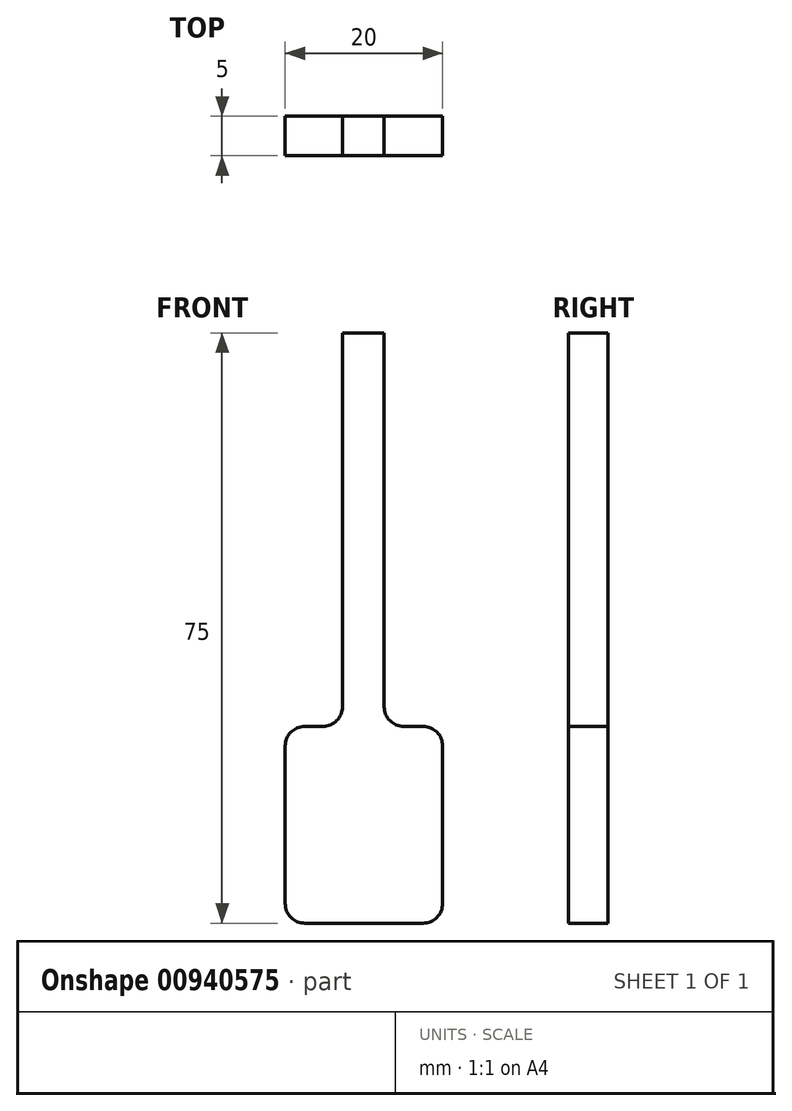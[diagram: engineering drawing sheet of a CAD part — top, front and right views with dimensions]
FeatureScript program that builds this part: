
annotation { "Feature Type Name" : "Feature", "Feature Type Description" : "" }
export const myFeature = defineFeature(function(context is Context, id is Id, definition is map)
    precondition{}
    {
        {
            var Q0;
            Q0=qCreatedBy(makeId("Front.planeOp"),FACE);
            var sketch = newSketch(context, id + "F0", { "sketchPlane" : qUnion([Q0])});
            skLineSegment(sketch, "E0.bottom", {"start": v(-7.5, -12.5) * mm, "end": v(7.5, -12.5) * mm});
            skLineSegment(sketch, "E0.left", {"start": v(-10, -10) * mm, "end": v(-10, 10) * mm});
            skLineSegment(sketch, "E0.right", {"start": v(10, -10) * mm, "end": v(10, 10) * mm});
            skPoint(sketch, "E0.middle", {"position": v(0, 0) * mm});
            skLineSegment(sketch, "E1.top", {"start": v(-2.72, 62.5) * mm, "end": v(2.57, 62.5) * mm});
            skLineSegment(sketch, "E1.left", {"start": v(-2.72, 15) * mm, "end": v(-2.72, 62.5) * mm});
            skLineSegment(sketch, "E1.right", {"start": v(2.57, 15) * mm, "end": v(2.57, 62.5) * mm});
            skLineSegment(sketch, "E2", {"start": v(-7.5, 12.5) * mm, "end": v(-5.22, 12.5) * mm});
            skLineSegment(sketch, "E3", {"start": v(5.07, 12.5) * mm, "end": v(7.5, 12.5) * mm});
            skPoint(sketch, "E4.visualSharp", {"position": v(-10, 12.5) * mm});
            skArc(sketch, "E4.filletArc", {"start": v(-7.5, 12.5) * mm, "mid": v(-9.27, 11.77) * mm, "end": v(-10, 10) * mm});
            skPoint(sketch, "E5.visualSharp", {"position": v(10, 12.5) * mm});
            skArc(sketch, "E5.filletArc", {"start": v(10, 10) * mm, "mid": v(9.27, 11.77) * mm, "end": v(7.5, 12.5) * mm});
            skPoint(sketch, "E6.visualSharp", {"position": v(2.57, 12.5) * mm});
            skArc(sketch, "E6.filletArc", {"start": v(2.57, 15) * mm, "mid": v(3.3, 13.23) * mm, "end": v(5.07, 12.5) * mm});
            skPoint(sketch, "E7.visualSharp", {"position": v(-2.72, 12.5) * mm});
            skArc(sketch, "E7.filletArc", {"start": v(-5.22, 12.5) * mm, "mid": v(-3.45, 13.23) * mm, "end": v(-2.72, 15) * mm});
            skPoint(sketch, "E8.visualSharp", {"position": v(10, -12.5) * mm});
            skArc(sketch, "E8.filletArc", {"start": v(7.5, -12.5) * mm, "mid": v(9.27, -11.77) * mm, "end": v(10, -10) * mm});
            skPoint(sketch, "E9.visualSharp", {"position": v(-10, -12.5) * mm});
            skArc(sketch, "E9.filletArc", {"start": v(-10, -10) * mm, "mid": v(-9.27, -11.77) * mm, "end": v(-7.5, -12.5) * mm});
            skSolve(sketch);
        }
        {
            var Q0;
            Q0=makeQuery(id+"F0.imprint","IMPRINT",FACE,{"disambiguationData":[TD([[makeQuery(id+"F0.imprint","IMPRINT",EDGE,{"derivedFrom":sQuery(id+"F0.wireOp",EDGE,"E0.bottom")}),1.0]])]});
            extrude(context, id + "F1", {"entities" : qUnion([Q0]), "depth" : 5 * mm, "offsetDistance" : 25 * mm});
        }
    });
